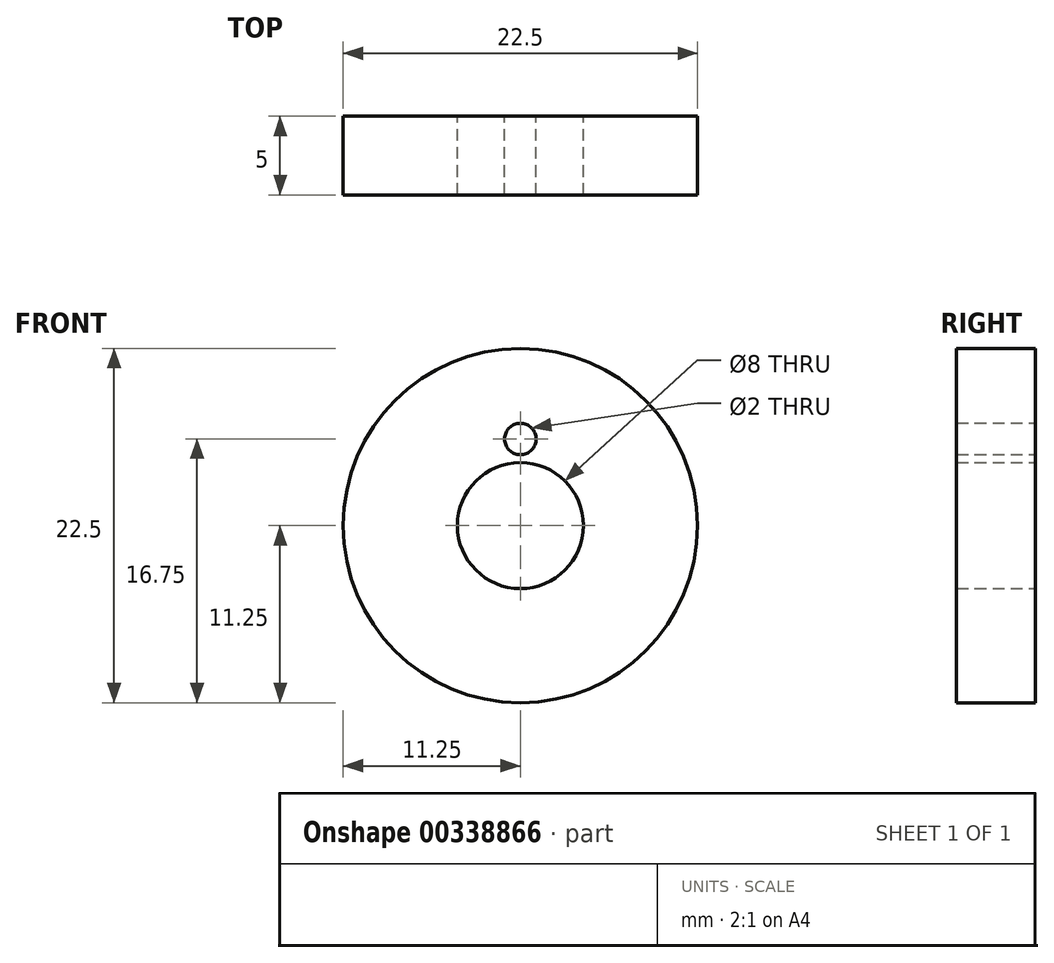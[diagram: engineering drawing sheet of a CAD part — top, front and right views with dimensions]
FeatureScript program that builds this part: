
annotation { "Feature Type Name" : "Feature", "Feature Type Description" : "" }
export const myFeature = defineFeature(function(context is Context, id is Id, definition is map)
    precondition{}
    {
        {
            var Q0;
            Q0=qCreatedBy(makeId("Front.planeOp"),FACE);
            var sketch = newSketch(context, id + "F0", { "sketchPlane" : qUnion([Q0])});
            skCircle(sketch, "E0", {"center": v(0, 0) * mm, "radius": 11.25 * mm});
            skCircle(sketch, "E1", {"center": v(0, 0) * mm, "radius": 4 * mm});
            skCircle(sketch, "E2", {"center": v(0, 5.5) * mm, "radius": 1 * mm});
            skSolve(sketch);
        }
        {
            var Q0;
            Q0 = qSketchRegion(id + "F0", true);
            extrude(context, id + "F1", {"entities" : qUnion([Q0]), "depth" : 5 * mm});
        }
    });
